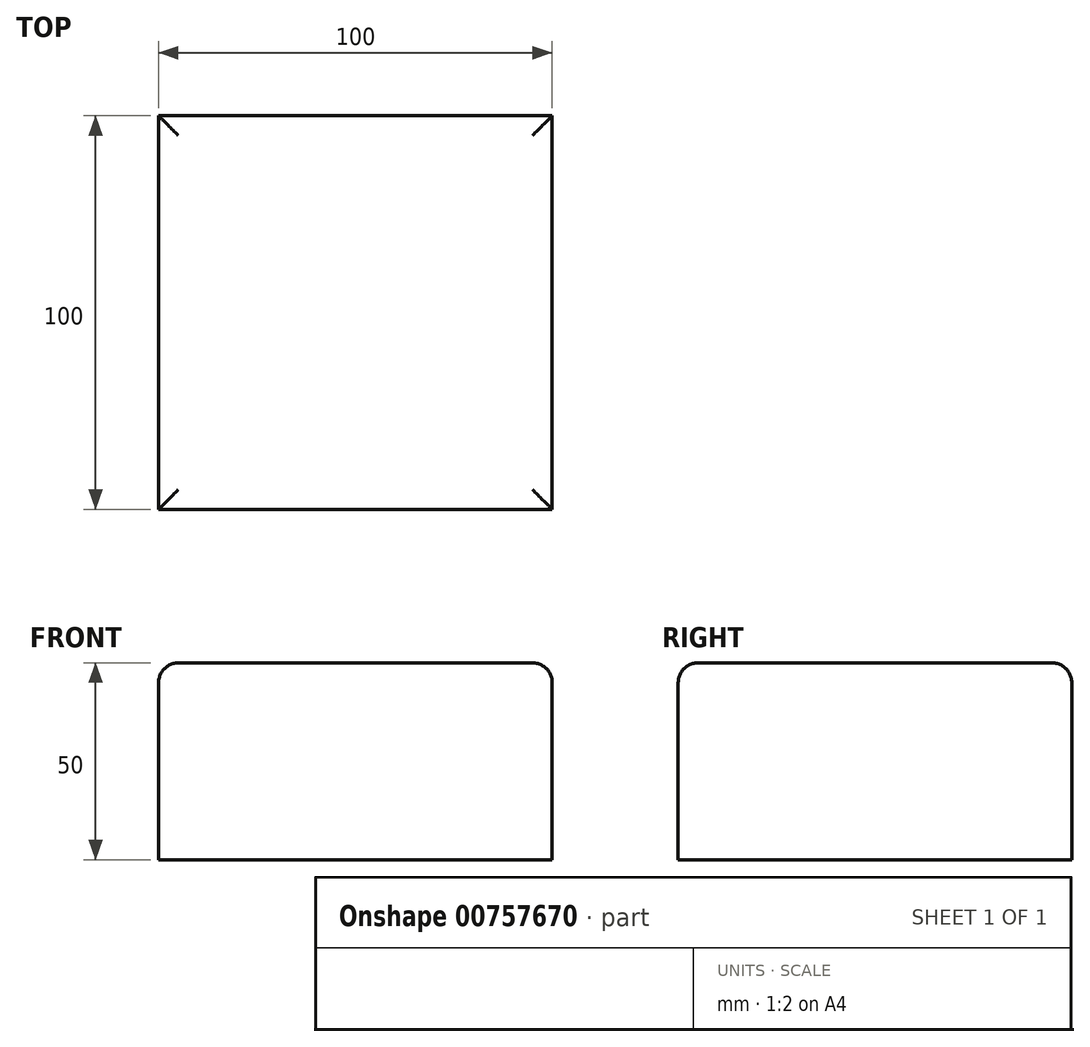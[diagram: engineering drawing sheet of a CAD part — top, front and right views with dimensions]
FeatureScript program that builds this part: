
annotation { "Feature Type Name" : "Feature", "Feature Type Description" : "" }
export const myFeature = defineFeature(function(context is Context, id is Id, definition is map)
    precondition{}
    {
        {
            var Q0;
            Q0=qCreatedBy(makeId("Top.planeOp"),FACE);
            var sketch = newSketch(context, id + "F0", { "sketchPlane" : qUnion([Q0])});
            skLineSegment(sketch, "E0.bottom", {"start": v(50, -50) * mm, "end": v(-50, -50) * mm});
            skLineSegment(sketch, "E0.top", {"start": v(50, 50) * mm, "end": v(-50, 50) * mm});
            skLineSegment(sketch, "E0.left", {"start": v(50, -50) * mm, "end": v(50, 50) * mm});
            skLineSegment(sketch, "E0.right", {"start": v(-50, -50) * mm, "end": v(-50, 50) * mm});
            skPoint(sketch, "E0.middle", {"position": v(0, 0) * mm});
            skSolve(sketch);
        }
        {
            var Q0;
            Q0=makeQuery(id+"F0.imprint","IMPRINT",FACE,{"disambiguationData":[TD([[makeQuery(id+"F0.imprint","IMPRINT",EDGE,{"derivedFrom":sQuery(id+"F0.wireOp",EDGE,"E0.bottom")}),-1.0]])]});
            extrude(context, id + "F1", {"entities" : qUnion([Q0]), "depth" : 50 * mm, "offsetDistance" : 25 * mm});
        }
        {
            var Q0;
            Q0=makeQuery(id+"F1.opExtrude","CAP_EDGE",EDGE,{"disambiguationData":[OSD([sQuery(id+"F0.wireOp",EDGE,"E0.bottom")])],"isStart":false});
            var Q1;
            Q1=makeQuery(id+"F1.opExtrude","CAP_EDGE",EDGE,{"disambiguationData":[OSD([sQuery(id+"F0.wireOp",EDGE,"E0.right")])],"isStart":false});
            var Q2;
            Q2=makeQuery(id+"F1.opExtrude","CAP_EDGE",EDGE,{"disambiguationData":[OSD([sQuery(id+"F0.wireOp",EDGE,"E0.left")])],"isStart":false});
            var Q3;
            Q3=makeQuery(id+"F1.opExtrude","CAP_EDGE",EDGE,{"disambiguationData":[OSD([sQuery(id+"F0.wireOp",EDGE,"E0.top")])],"isStart":false});
            fillet(context, id + "F2", {"entities" : qUnion([Q0, Q1, Q2, Q3]), "radius" : 5 * mm, "tangentPropagation" : true, "allowEdgeOverflow" : false});
        }
    });
